# Revit family: 63_UN_LF_SM_Code MEN6
name_source: partatom
category: Lighting Fixtures
units: mm (PartAtom-declared; Revit-internal decimal feet)

## family parameters
Always vertical = Yes
Cut with Voids When Loaded = Yes
Light Source = No
OmniClass Number = 23.80.70.11.14
OmniClass Title = General Luminaries, Directional
Part Type = Normal
Room Calculation Point = Yes
Round Connector Dimension = Use Diameter
Shared = No
Work Plane-Based = No

## types (4) — shared parameters
Assembly Code = 63.0
Housing_Material = Plastic, Opaque Black
IfcExportAs = IfcLightFixtureType
IfcExportType = USERDEFINED
Lamp = LED
Manufacturer = Light International
URL = https://lightinternational.nl
Voltage = 230 V

## per-type parameters (varying)
| type | Apparent Load | Light Source | Lightsource_tilt | Luminous Flux (lm) | Model | Type Comments | Wattage Comments |
| MEN61 - Wall mounted | 8 VA | MEN6 Geometry : MEN61 | 90.00° | 1100 lm | MEN61 | MEN61 | 7.9W |
| MEN61 - Ceiling mounted | 8 VA | MEN6 Geometry : MEN61 | 180.00° | 1100 lm | MEN61 | MEN61 | 7.9W |
| MEN62 - Ceiling mounted | 18 VA | MEN6 Geometry : MEN62 | 180.00° | 2500 lm | MEN62 | MEN62 | 17.6W |
| MEN62 - Wall mounted | 18 VA | MEN6 Geometry : MEN62 | 90.00° | 2500 lm | MEN62 | MEN62 | 17.6W |

## geometry (parser evidence)
native form markers: Sweep x15
no freeform markers — native parametric forms only
